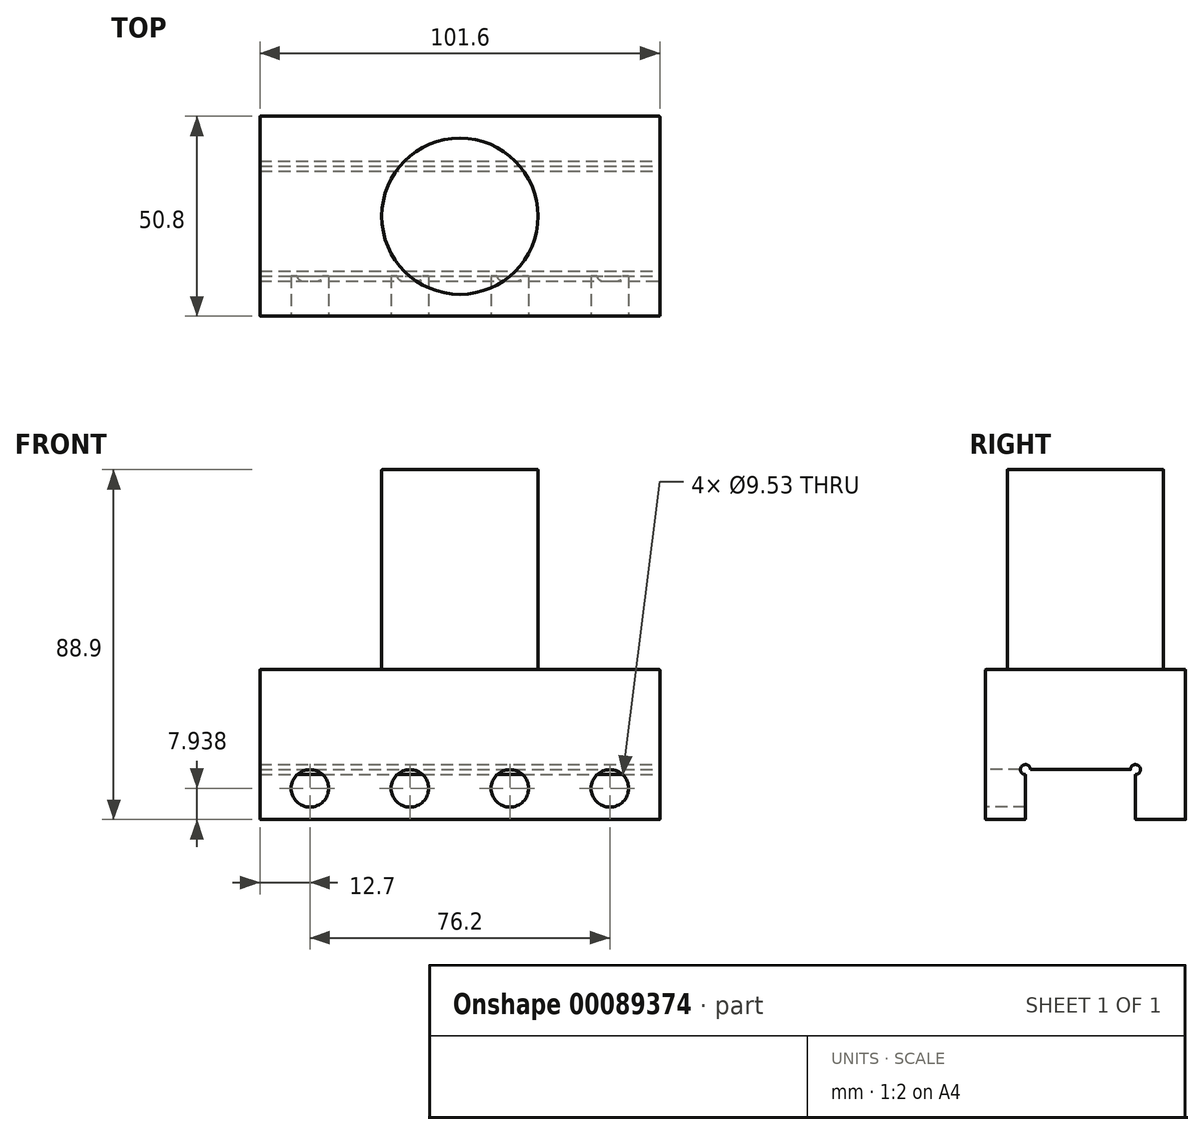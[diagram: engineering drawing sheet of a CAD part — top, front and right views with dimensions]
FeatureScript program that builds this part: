
annotation { "Feature Type Name" : "Feature", "Feature Type Description" : "" }
export const myFeature = defineFeature(function(context is Context, id is Id, definition is map)
    precondition{}
    {
        {
            var Q0;
            Q0=qCreatedBy(makeId("Right.planeOp"),FACE);
            var sketch = newSketch(context, id + "F0", { "sketchPlane" : qUnion([Q0])});
            skLineSegment(sketch, "E0", {"start": v(0, 0) * mm, "end": v(0, 38.1) * mm});
            skLineSegment(sketch, "E1", {"start": v(0, 38.1) * mm, "end": v(50.8, 38.1) * mm});
            skLineSegment(sketch, "E2", {"start": v(50.8, 38.1) * mm, "end": v(50.8, 0) * mm});
            skLineSegment(sketch, "E3", {"start": v(50.8, 0) * mm, "end": v(38.1, 0) * mm});
            skLineSegment(sketch, "E4", {"start": v(38.1, 0) * mm, "end": v(38.1, 11.43) * mm});
            skLineSegment(sketch, "E5", {"start": v(36.83, 12.7) * mm, "end": v(11.43, 12.7) * mm});
            skLineSegment(sketch, "E6", {"start": v(10.16, 11.43) * mm, "end": v(10.16, 0) * mm});
            skLineSegment(sketch, "E7", {"start": v(10.16, 0) * mm, "end": v(0, 0) * mm});
            skArc(sketch, "E8", {"start": v(11.43, 12.7) * mm, "mid": v(9.26, 13.6) * mm, "end": v(10.16, 11.43) * mm});
            skArc(sketch, "E9", {"start": v(38.1, 11.43) * mm, "mid": v(39, 13.6) * mm, "end": v(36.83, 12.7) * mm});
            skSolve(sketch);
        }
        {
            var Q0;
            Q0=qSketchRegion(id+"F0",true);
            extrude(context, id + "F1", {"entities" : qUnion([Q0]), "oppositeDirection" : true, "depth" : 101.6 * mm});
        }
        {
            var Q0;
            Q0=makeQuery(id+"F1.opExtrude","SWEPT_FACE",FACE,{"disambiguationData":[OSD([sQuery(id+"F0.wireOp",EDGE,"E1")])]});
            var sketch = newSketch(context, id + "F2", { "sketchPlane" : qUnion([Q0])});
            skCircle(sketch, "E10", {"center": v(-50.8, 25.4) * mm, "radius": 19.84 * mm});
            skLineSegment(sketch, "E11", {"start": v(-50.8, 25.4) * mm, "end": v(0, 25.4) * mm});
            skLineSegment(sketch, "E12", {"start": v(-50.8, 25.4) * mm, "end": v(-101.6, 25.4) * mm});
            skPoint(sketch, "E12.endSnap0", {"position": v(-101.6, 25.4) * mm});
            skLineSegment(sketch, "E13", {"start": v(-50.8, 50.8) * mm, "end": v(-50.8, 25.4) * mm});
            skLineSegment(sketch, "E14", {"start": v(-50.8, 25.4) * mm, "end": v(-50.8, 0) * mm});
            skSolve(sketch);
        }
        {
            var Q0;
            Q0=qSketchRegion(id+"F2",true);
            extrude(context, id + "F3", {"entities" : qUnion([Q0]), "operationType" : NewBodyOperationType.ADD, "depth" : 50.8 * mm});
        }
        {
            var Q0;
            Q0=makeQuery(id+"F1.opExtrude","SWEPT_FACE",FACE,{"disambiguationData":[OSD([sQuery(id+"F0.wireOp",EDGE,"E0")])]});
            var sketch = newSketch(context, id + "F4", { "sketchPlane" : qUnion([Q0])});
            skCircle(sketch, "E15", {"center": v(-12.7, 7.94) * mm, "radius": 4.76 * mm});
            skCircle(sketch, "E16", {"center": v(-38.1, 7.94) * mm, "radius": 4.76 * mm});
            skCircle(sketch, "E17", {"center": v(-63.5, 7.94) * mm, "radius": 4.76 * mm});
            skCircle(sketch, "E18", {"center": v(-88.9, 7.94) * mm, "radius": 4.76 * mm});
            skLineSegment(sketch, "E19", {"start": v(-12.7, 7.94) * mm, "end": v(0, 7.94) * mm});
            skLineSegment(sketch, "E20", {"start": v(-88.9, 7.94) * mm, "end": v(-101.6, 7.94) * mm});
            skSolve(sketch);
        }
        {
            var Q0;
            Q0=qSketchRegion(id+"F4",true);
            extrude(context, id + "F5", {"entities" : qUnion([Q0]), "operationType" : NewBodyOperationType.REMOVE, "endBound" : BoundingType.UP_TO_NEXT, "oppositeDirection" : true, "depth" : 25.4 * mm});
        }
        {
            var Q0;
            Q0=qSketchRegion(id+"F4",true);
            extrude(context, id + "F6", {"entities" : qUnion([Q0]), "operationType" : NewBodyOperationType.REMOVE, "endBound" : BoundingType.UP_TO_NEXT, "oppositeDirection" : true, "depth" : 25.4 * mm});
        }
        {
            var Q0;
            Q0=makeQuery(id+"F3.opExtrude","CAP_EDGE",EDGE,{"disambiguationData":[OSD([sQuery(id+"F2.wireOp",EDGE,"E10")])],"isStart":false});
            var Q1;
            Q1=makeQuery(id+"F3.opExtrude","CAP_EDGE",EDGE,{"disambiguationData":[OSD([sQuery(id+"F2.wireOp",EDGE,"E10")])],"isStart":true});
            var Q2;
            Q2=makeQuery(id+"F1.opExtrude","SWEPT_EDGE",EDGE,{"disambiguationData":[OSD([sQuery(id+"F0.wireOp",EDGE,"E0"),sQuery(id+"F0.wireOp",EDGE,"E1")])]});
            var Q3;
            Q3=makeQuery(id+"F1.opExtrude","CAP_EDGE",EDGE,{"disambiguationData":[OSD([sQuery(id+"F0.wireOp",EDGE,"E0")])],"isStart":true});
            var Q4;
            Q4=makeQuery(id+"F1.opExtrude","CAP_EDGE",EDGE,{"disambiguationData":[OSD([sQuery(id+"F0.wireOp",EDGE,"E1")])],"isStart":true});
            var Q5;
            Q5=makeQuery(id+"F1.opExtrude","SWEPT_EDGE",EDGE,{"disambiguationData":[OSD([sQuery(id+"F0.wireOp",EDGE,"E1"),sQuery(id+"F0.wireOp",EDGE,"E2")])]});
            var Q6;
            Q6=makeQuery(id+"F1.opExtrude","CAP_EDGE",EDGE,{"disambiguationData":[OSD([sQuery(id+"F0.wireOp",EDGE,"E1")])],"isStart":false});
            var Q7;
            Q7=makeQuery(id+"F1.opExtrude","CAP_EDGE",EDGE,{"disambiguationData":[OSD([sQuery(id+"F0.wireOp",EDGE,"E0")])],"isStart":false});
            var Q8;
            Q8=makeQuery(id+"F1.opExtrude","SWEPT_EDGE",EDGE,{"disambiguationData":[OSD([sQuery(id+"F0.wireOp",EDGE,"E0"),sQuery(id+"F0.wireOp",EDGE,"E7")])]});
            var Q9;
            Q9=makeQuery(id+"F1.opExtrude","CAP_EDGE",EDGE,{"disambiguationData":[OSD([sQuery(id+"F0.wireOp",EDGE,"E3")])],"isStart":true});
            var Q10;
            Q10=makeQuery(id+"F1.opExtrude","CAP_EDGE",EDGE,{"disambiguationData":[OSD([sQuery(id+"F0.wireOp",EDGE,"E7")])],"isStart":true});
            var Q11;
            Q11=makeQuery(id+"F1.opExtrude","CAP_EDGE",EDGE,{"disambiguationData":[OSD([sQuery(id+"F0.wireOp",EDGE,"E2")])],"isStart":true});
            var Q12;
            Q12=makeQuery(id+"F1.opExtrude","CAP_EDGE",EDGE,{"disambiguationData":[OSD([sQuery(id+"F0.wireOp",EDGE,"E5")])],"isStart":true});
            var Q13;
            Q13=makeQuery(id+"F1.opExtrude","CAP_EDGE",EDGE,{"disambiguationData":[OSD([sQuery(id+"F0.wireOp",EDGE,"E4")])],"isStart":true});
            var Q14;
            Q14=makeQuery(id+"F1.opExtrude","CAP_EDGE",EDGE,{"disambiguationData":[OSD([sQuery(id+"F0.wireOp",EDGE,"E6")])],"isStart":true});
            var Q15;
            Q15=makeQuery(id+"F1.opExtrude","CAP_EDGE",EDGE,{"disambiguationData":[OSD([sQuery(id+"F0.wireOp",EDGE,"E2")])],"isStart":false});
            var Q16;
            Q16=makeQuery(id+"F1.opExtrude","CAP_EDGE",EDGE,{"disambiguationData":[OSD([sQuery(id+"F0.wireOp",EDGE,"E3")])],"isStart":false});
            var Q17;
            Q17=makeQuery(id+"F1.opExtrude","CAP_EDGE",EDGE,{"disambiguationData":[OSD([sQuery(id+"F0.wireOp",EDGE,"E5")])],"isStart":false});
            var Q18;
            Q18=makeQuery(id+"F1.opExtrude","CAP_EDGE",EDGE,{"disambiguationData":[OSD([sQuery(id+"F0.wireOp",EDGE,"E4")])],"isStart":false});
            var Q19;
            Q19=makeQuery(id+"F1.opExtrude","CAP_EDGE",EDGE,{"disambiguationData":[OSD([sQuery(id+"F0.wireOp",EDGE,"E6")])],"isStart":false});
            var Q20;
            Q20=makeQuery(id+"F1.opExtrude","CAP_EDGE",EDGE,{"disambiguationData":[OSD([sQuery(id+"F0.wireOp",EDGE,"E7")])],"isStart":false});
            var Q21;
            Q21=makeQuery(id+"F1.opExtrude","SWEPT_EDGE",EDGE,{"disambiguationData":[OSD([sQuery(id+"F0.wireOp",EDGE,"E3"),sQuery(id+"F0.wireOp",EDGE,"E4")])]});
            var Q22;
            Q22=makeQuery(id+"F1.opExtrude","SWEPT_EDGE",EDGE,{"disambiguationData":[OSD([sQuery(id+"F0.wireOp",EDGE,"E6"),sQuery(id+"F0.wireOp",EDGE,"E7")])]});
            fillet(context, id + "F7", {"entities" : qUnion([Q0, Q1, Q2, Q3, Q4, Q5, Q6, Q7, Q8, Q9, Q10, Q11, Q12, Q13, Q14, Q15, Q16, Q17, Q18, Q19, Q20, Q21, Q22]), "radius" : 0.13 * mm, "tangentPropagation" : true, "allowEdgeOverflow" : false});
        }
    });
